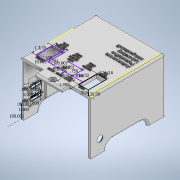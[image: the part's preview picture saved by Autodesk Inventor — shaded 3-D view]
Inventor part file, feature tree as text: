
AUTODESK INVENTOR PART (.ipt)
format: ipt  version: 2020 (Build 240168000, 168)  size: 3,253,248 bytes
history: native  units: in
note: dims shown in document units (in); Inventor stores cm internally (conversion verified against a paired STEP export)
features: sketch x15, extrude x14, projected_geometry x4, hole x3, fillet x3
ambient origin geometry x8: Origin, YZ Plane, XZ Plane, XY Plane, X Axis, Y Axis, Z Axis, Center Point
bodies: Solid1 (feature_tree)
feature tree (39):
  extrude  "Extrusion1"  Depth=5.4in
  hole  "Hole1"  [1 undecoded]
  extrude  "Extrusion2"  Depth=0.55in
  extrude  "Extrusion3"  Depth=0.95in
  fillet  "Fillet1"  Radius=0.18in
  sketch  "Sketch5"  dims[d9=0.266in d10=0.25in d11=0.438in d12=0.0625in d13=0.5635in d14=0.25in d15=0.8108in d16=0.18in]
  extrude  "Extrusion4"  Depth=0.18in
  sketch  "Sketch7"  dims[d19=3.675in d20=0.0in d21=1.0in]
  hole  "Hole3"  [1 undecoded]
  extrude  "Extrusion5"  Depth=10.0in TaperAngle=0.0deg
  extrude  "Extrusion6"  Depth=0.125in
  hole  "Hole4"  [1 undecoded]
  extrude  "Extrusion7"  Depth=1.0in
  extrude  "Extrusion8"  Depth=0.5in
  extrude  "Extrusion9"  Depth=0.6875in
  extrude  "Extrusion10"  Depth=1.0in
  fillet  "Fillet2"  [1 undecoded]
  extrude  "Extrusion11"  Depth=0.125in TaperAngle=0.0deg
  sketch  "Sketch14"  dims[d43=1.3438in d44=1.0in d47=180.0deg]
  extrude  "Extrusion12"  Depth=0.125in TaperAngle=0.0deg
  extrude  "Extrusion13"  Depth=0.125in
  extrude  "Extrusion14"  Depth=0.125in
  fillet  "Fillet3"  Radius=0.5in
  sketch  "Sketch1"  dims[d0=5.0in d1=5.4in]
  sketch  "Sketch2"  dims[d2=1.6in d3=180.0deg]
  sketch  "Sketch3"  dims[d4=1.9in d5=0.55in]
  sketch  "Sketch4"  dims[d6=0.2in d7=0.0in d8=0.95in]
  sketch  "Sketch6"  dims[d17=0.18in d18=0.18in]
  sketch  "Sketch8"  dims[d22=1.0in d23=10.0in d24=0.0in]
  sketch  "Sketch9"  dims[d25=0.125in d26=0.5in]
  sketch  "Sketch10"  dims[d27=1.0625in d28=1.0625in]
  sketch  "Sketch11"  dims[d29=180.0deg d37=1.0in]
  sketch  "Sketch12"  dims[d38=0.2in d39=0.0in d40=0.5in]
  sketch  "Sketch13"  dims[d41=135.0deg d42=0.6875in]
  sketch  "Sketch15"  dims[d49=180.0deg d54=0.1575in d55=0.75in d56=0.385in d57=0.25in d58=0.5635in d59=1.0in d60=0.8108in d61=0.2in d62=0.0in d63=0.15in d64=0.0in d65=1.2405in d66=0.0in d67=0.5in d68=0.0in d69=0.5in d70=0.5in d71=0.5in d72=0.0in d73=0.25in d74=45.0deg d75=0.4331in d76=0.75in d77=0.385in d78=0.25in d79=0.5635in d80=1.0in d81=0.8108in d82=0.075in d83=0.075in d84=0.15in d85=0.0in d86=0.225in d87=0.1in d88=0.0in d89=0.225in d90=0.1in d91=0.0in d92=0.75in d93=0.15in d94=0.0in d95=0.0625in d98=0.5in d99=0.875in d100=1.1875in d101=0.5in d102=0.75in d103=0.05in d104=0.0in d115=1.0in d116=90.0deg d117=1.0in d118=90.0deg d119=0.0in d120=0.75in d121=180.0deg d122=0.8in d123=0.45in d124=0.45in d125=1.0in d126=0.1in d127=1.0in d128=0.1in d129=0.1in d130=0.0in d131=1.5in d132=1.25in d133=1.75in d134=0.1in d135=0.0in d136=0.05in d137=0.0in d138=0.125in]
  projected_geometry  "Projected Loop1"
  projected_geometry  "Projected Loop2"
  projected_geometry  "Projected Loop3"
  projected_geometry  "Projected Loop4"
note: 4 required parameter values undecoded (feature->parameter linkage not recoverable at this tier; creation-order binding heuristic only, values carry confidence <= 0.55)
